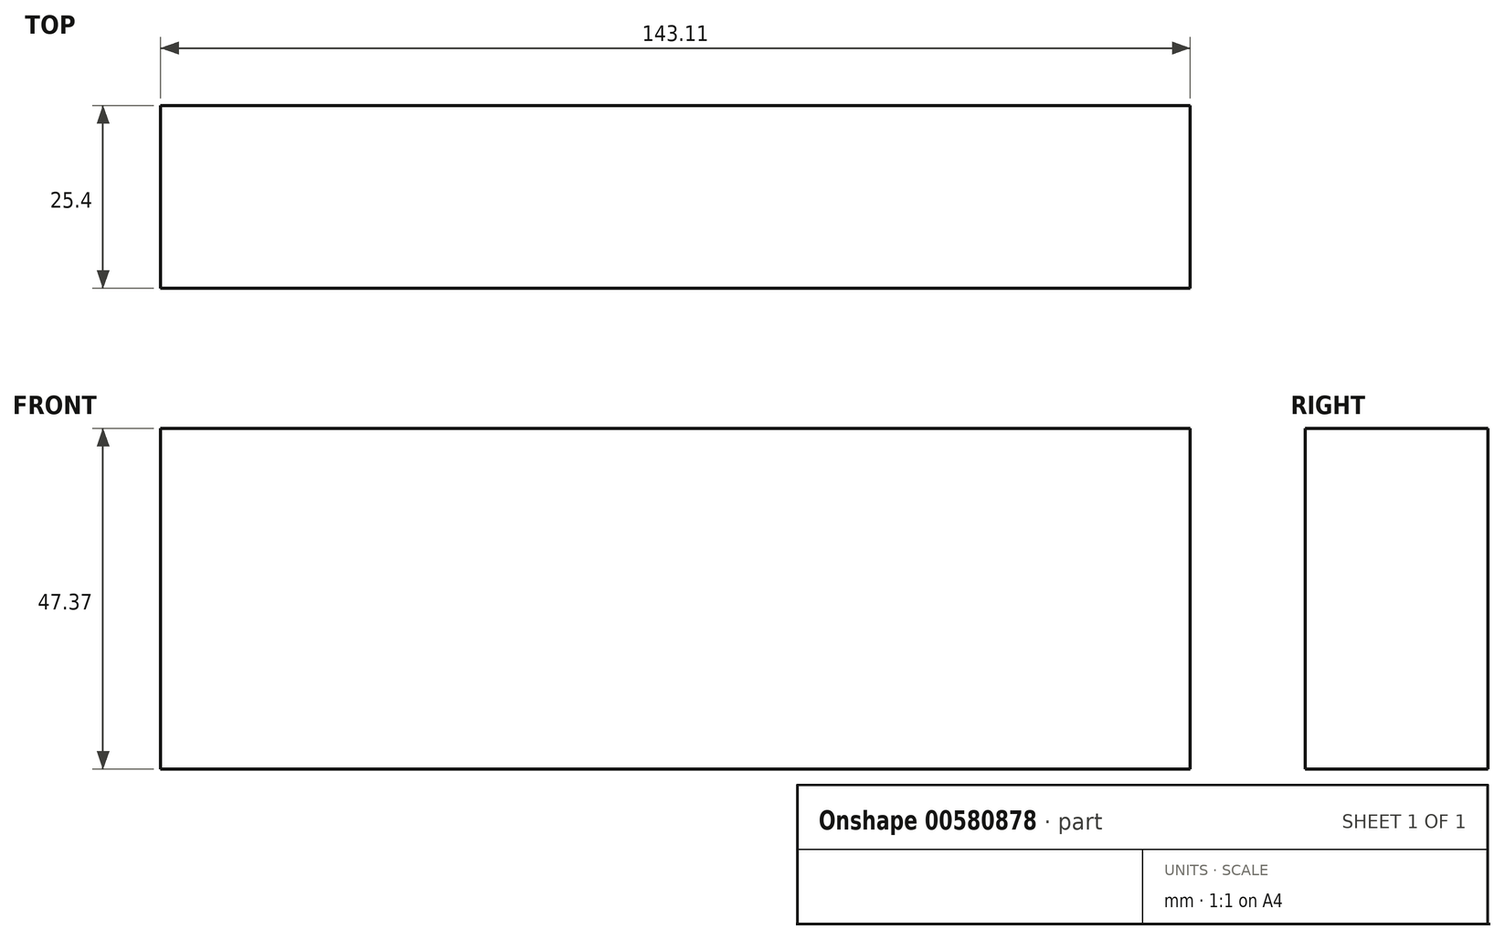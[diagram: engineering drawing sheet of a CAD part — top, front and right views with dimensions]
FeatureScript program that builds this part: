
annotation { "Feature Type Name" : "Feature", "Feature Type Description" : "" }
export const myFeature = defineFeature(function(context is Context, id is Id, definition is map)
    precondition{}
    {
        {
            var Q0;
            Q0=qCreatedBy(makeId("Front.planeOp"),FACE);
            var sketch = newSketch(context, id + "F0", { "sketchPlane" : qUnion([Q0])});
            skLineSegment(sketch, "E0.bottom", {"start": v(-137.46, 42.32) * mm, "end": v(5.65, 42.32) * mm});
            skLineSegment(sketch, "E0.top", {"start": v(-137.46, -5.05) * mm, "end": v(5.65, -5.05) * mm});
            skLineSegment(sketch, "E0.left", {"start": v(-137.46, 42.32) * mm, "end": v(-137.46, -5.05) * mm});
            skLineSegment(sketch, "E0.right", {"start": v(5.65, 42.32) * mm, "end": v(5.65, -5.05) * mm});
            skSolve(sketch);
        }
        {
            var Q0;
            Q0=makeQuery(id+"F0.imprint","IMPRINT",FACE,{"disambiguationData":[TD([[makeQuery(id+"F0.imprint","IMPRINT",EDGE,{"derivedFrom":sQuery(id+"F0.wireOp",EDGE,"E0.bottom")}),-1.0]])]});
            extrude(context, id + "F1", {"entities" : qUnion([Q0]), "depth" : 25.4 * mm, "offsetDistance" : 25.4 * mm});
        }
    });
